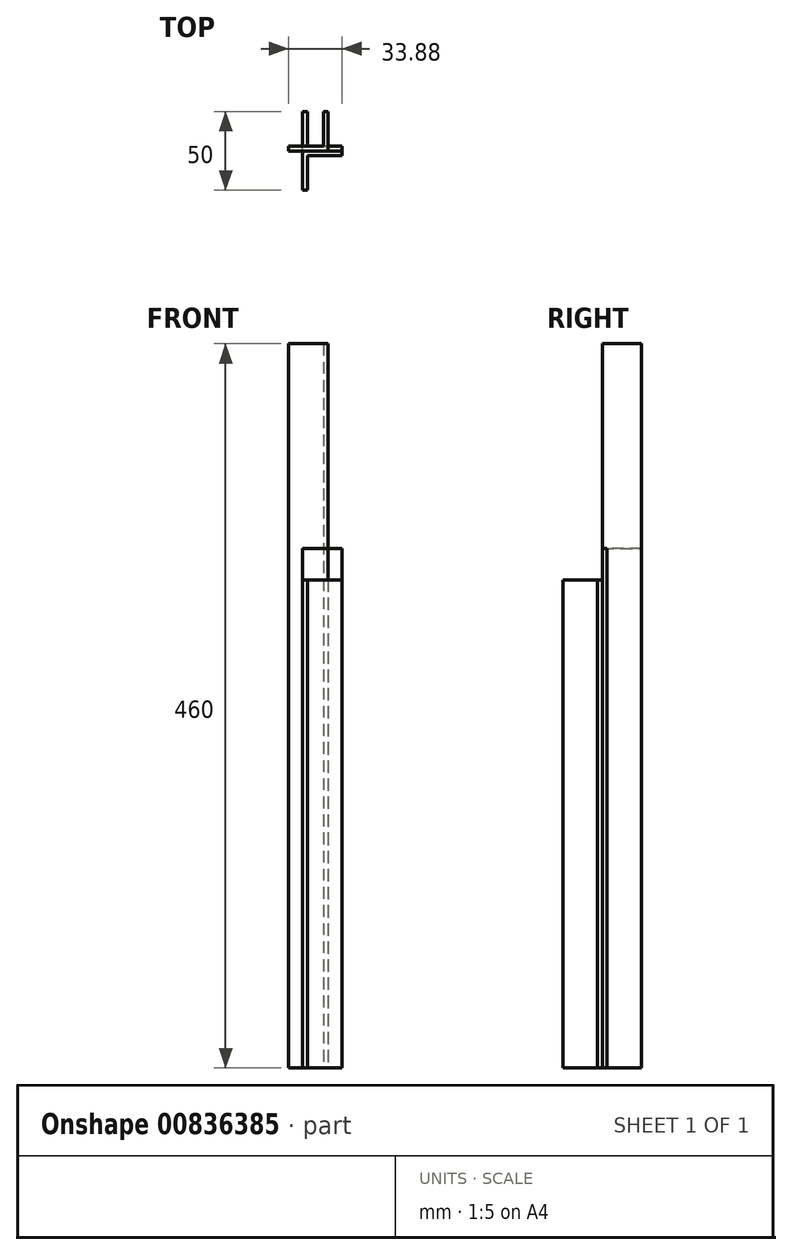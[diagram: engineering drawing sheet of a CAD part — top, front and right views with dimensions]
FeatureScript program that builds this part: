
annotation { "Feature Type Name" : "Feature", "Feature Type Description" : "" }
export const myFeature = defineFeature(function(context is Context, id is Id, definition is map)
    precondition{}
    {
        {
            var Q0;
            Q0=qCreatedBy(makeId("Front.planeOp"),FACE);
            var sketch = newSketch(context, id + "F0", { "sketchPlane" : qUnion([Q0])});
            skLineSegment(sketch, "E0", {"start": v(0, 0) * mm, "end": v(0, 25) * mm});
            skLineSegment(sketch, "E1", {"start": v(0, 25) * mm, "end": v(-3, 25) * mm});
            skLineSegment(sketch, "E2", {"start": v(-3, 25) * mm, "end": v(-3, 3) * mm});
            skLineSegment(sketch, "E3", {"start": v(-3, 3) * mm, "end": v(-25, 3) * mm});
            skLineSegment(sketch, "E4", {"start": v(-25, 3) * mm, "end": v(-25, 0) * mm});
            skLineSegment(sketch, "E5", {"start": v(-25, 0) * mm, "end": v(0, 0) * mm});
            skSolve(sketch);
        }
        {
            var Q0;
            Q0=qCreatedBy(makeId("Top.planeOp"),FACE);
            var sketch = newSketch(context, id + "F1", { "sketchPlane" : qUnion([Q0])});
            skLineSegment(sketch, "E6", {"start": v(0, 0) * mm, "end": v(0, 25) * mm});
            skLineSegment(sketch, "E7", {"start": v(0, 25) * mm, "end": v(3, 25) * mm});
            skLineSegment(sketch, "E8", {"start": v(3, 25) * mm, "end": v(3, 3) * mm});
            skLineSegment(sketch, "E9", {"start": v(3, 3) * mm, "end": v(25, 3) * mm});
            skLineSegment(sketch, "E10", {"start": v(25, 3) * mm, "end": v(25, 0) * mm});
            skLineSegment(sketch, "E11", {"start": v(25, 0) * mm, "end": v(0, 0) * mm});
            skSolve(sketch);
        }
        {
            var Q0;
            Q0=qCreatedBy(makeId("Top.planeOp"),FACE);
            var sketch = newSketch(context, id + "F2", { "sketchPlane" : qUnion([Q0])});
            skLineSegment(sketch, "E12", {"start": v(16.12, 0) * mm, "end": v(16.12, 25) * mm});
            skLineSegment(sketch, "E13", {"start": v(16.12, 25) * mm, "end": v(13.12, 25) * mm});
            skLineSegment(sketch, "E14", {"start": v(13.12, 25) * mm, "end": v(13.12, 3) * mm});
            skLineSegment(sketch, "E15", {"start": v(13.12, 3) * mm, "end": v(-8.88, 3) * mm});
            skLineSegment(sketch, "E16", {"start": v(-8.88, 3) * mm, "end": v(-8.88, 0) * mm});
            skLineSegment(sketch, "E17", {"start": v(-8.88, 0) * mm, "end": v(16.12, 0) * mm});
            skSolve(sketch);
        }
        {
            var Q0;
            Q0 = qSketchRegion(id + "F0", true);
            extrude(context, id + "F3", {"entities" : qUnion([Q0]), "depth" : 310 * mm, "offsetDistance" : 25 * mm});
        }
        {
            var Q0;
            Q0 = qSketchRegion(id + "F1", true);
            extrude(context, id + "F4", {"entities" : qUnion([Q0]), "depth" : 330 * mm, "offsetDistance" : 25 * mm});
        }
        {
            var Q0;
            Q0=makeQuery(id+"F3.opExtrude","SWEPT_BODY",BODY,{"disambiguationData":[OSD([sQuery(id+"F0.wireOp",EDGE,"E0"),sQuery(id+"F0.wireOp",EDGE,"E1"),sQuery(id+"F0.wireOp",EDGE,"E2"),sQuery(id+"F0.wireOp",EDGE,"E3"),sQuery(id+"F0.wireOp",EDGE,"E4"),sQuery(id+"F0.wireOp",EDGE,"E5")])]});
            var Q1;
            Q1=makeQuery(id+"F3.opExtrude","CAP_EDGE",EDGE,{"disambiguationData":[OSD([sQuery(id+"F0.wireOp",EDGE,"E5")])],"isStart":true});
            transform(context, id + "F5", {"entities" : qUnion([Q0]), "transformType" : TransformType.ROTATION, "transformAxis" : qUnion([Q1]), "angle" : 90 * degree, "oppositeDirection" : true, "makeCopy" : false});
        }
        {
            var Q0;
            Q0=makeQuery(id+"F3.opExtrude","SWEPT_BODY",BODY,{"disambiguationData":[OSD([sQuery(id+"F0.wireOp",EDGE,"E0"),sQuery(id+"F0.wireOp",EDGE,"E1"),sQuery(id+"F0.wireOp",EDGE,"E2"),sQuery(id+"F0.wireOp",EDGE,"E3"),sQuery(id+"F0.wireOp",EDGE,"E4"),sQuery(id+"F0.wireOp",EDGE,"E5")])]});
            var Q1;
            Q1=makeQuery(id+"F3.opExtrude","SWEPT_EDGE",EDGE,{"disambiguationData":[OSD([sQuery(id+"F0.wireOp",EDGE,"E0"),sQuery(id+"F0.wireOp",EDGE,"E5")])]});
            transform(context, id + "F6", {"entities" : qUnion([Q0]), "transformType" : TransformType.ROTATION, "transformAxis" : qUnion([Q1]), "angle" : 180 * degree, "makeCopy" : false});
        }
        {
            var Q0;
            Q0 = qSketchRegion(id + "F2", true);
            extrude(context, id + "F7", {"entities" : qUnion([Q0]), "depth" : 460 * mm, "offsetDistance" : 25 * mm});
        }
    });
